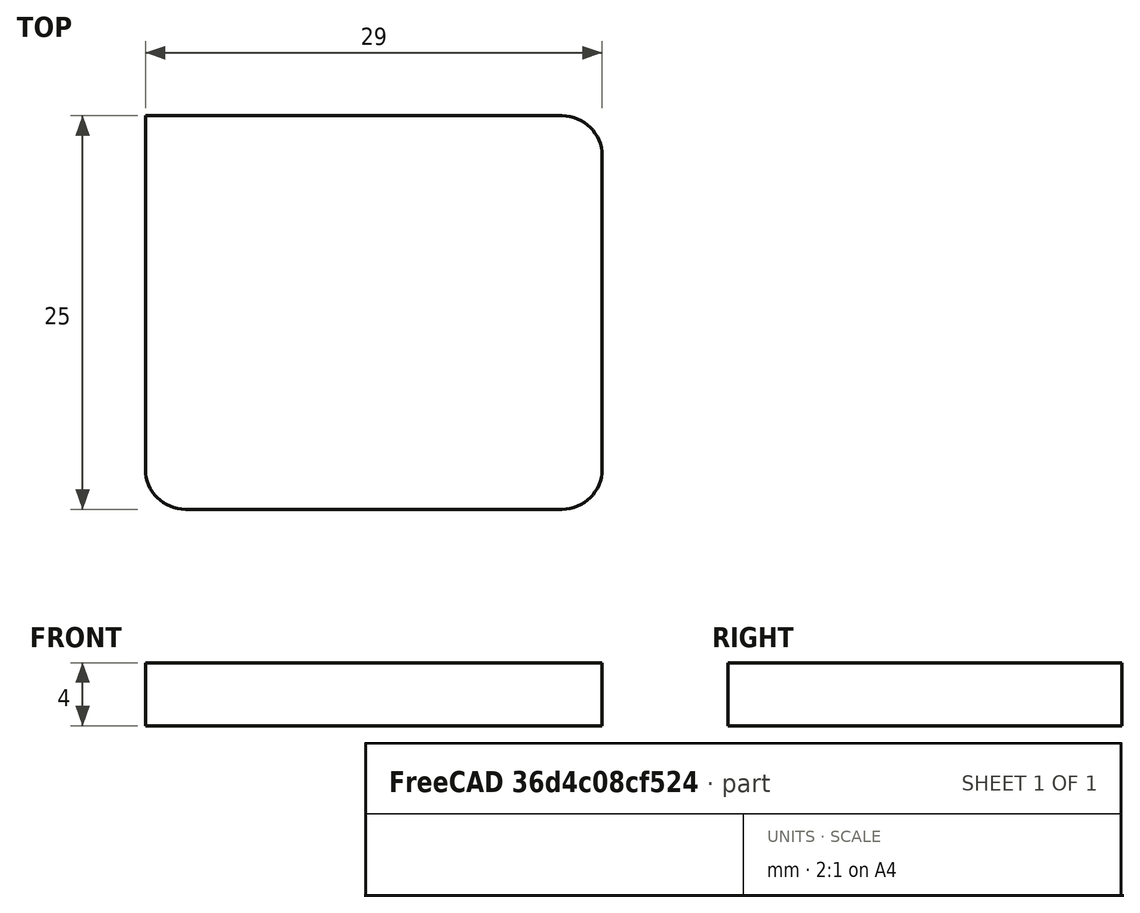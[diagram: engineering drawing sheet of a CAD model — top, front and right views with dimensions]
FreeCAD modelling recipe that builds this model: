
FCSTD DOCUMENT  (FreeCAD 1.0R39109 (Git))
Label: lora_rfm9x
License: All rights reserved
LicenseURL: http://en.wikipedia.org/wiki/All_rights_reserved
objects: Sketcher::SketchObject×1, PartDesign::Pad×1, PartDesign::Body×1
note: 6 computed .brp shape members not serialized (recipe doc carries the construction recipe); baked Part::Feature solids carry a one-line shape summary decoded from their .brp

FEATURE [Sketcher::SketchObject] Sketch
  ArcFitTolerance = 0
  AttachmentSupport = -> [XY_Plane]
  FullyConstrained = true
  MakeInternals = false
  MapMode = 5
  sketch-geometry (10):
    g0: LineSegment StartX=-14.5 StartY=12.5 StartZ=0 EndX=11.96 EndY=12.5 EndZ=0
    g1: LineSegment StartX=14.5 StartY=9.96 StartZ=0 EndX=14.5 EndY=-9.96 EndZ=0
    g2: LineSegment StartX=11.96 StartY=-12.5 StartZ=0 EndX=-11.96 EndY=-12.5 EndZ=0
    g3: LineSegment StartX=-14.5 StartY=-9.96 StartZ=0 EndX=-14.5 EndY=12.5 EndZ=0
    g4: ArcOfCircle CenterX=11.96 CenterY=-9.96 CenterZ=0 NormalX=0 NormalY=0 NormalZ=1 AngleXU=0 Radius=2.54 StartAngle=4.71239 EndAngle=6.28319
    g5: GeomPoint [constr] X=14.5 Y=-12.5 Z=0
    g6: ArcOfCircle CenterX=11.96 CenterY=9.96 CenterZ=0 NormalX=0 NormalY=0 NormalZ=1 AngleXU=0 Radius=2.54 StartAngle=0 EndAngle=1.5708
    g7: GeomPoint [constr] X=14.5 Y=12.5 Z=0
    g8: ArcOfCircle CenterX=-11.96 CenterY=-9.96 CenterZ=0 NormalX=0 NormalY=0 NormalZ=1 AngleXU=0 Radius=2.54 StartAngle=3.14159 EndAngle=4.71239
    g9: GeomPoint [constr] X=-14.5 Y=-12.5 Z=0
  constraints (23):
    c: Coincident(g3,g0)
    c: Horizontal(g0)
    c: Horizontal(g2)
    c: Vertical(g1)
    c: Vertical(g3)
    c: PointOnObject(g5,g2)
    c: PointOnObject(g5,g1)
    c: Tangent(g2,g4) = 1.5708
    c: Tangent(g1,g4) = 1.5708
    c: PointOnObject(g7,g1)
    c: PointOnObject(g7,g0)
    c: Tangent(g1,g6) = 1.5708
    c: Tangent(g0,g6) = 1.5708
    c: PointOnObject(g9,g3)
    c: PointOnObject(g9,g2)
    c: Tangent(g3,g8) = 1.5708
    c: Tangent(g2,g8) = 1.5708
    c: Symmetric(g0,g5,g-1)
    c: DistanceX(g0,g7) = 29
    c: DistanceY(g5,g7) = 25
    c: Equal(g6,g4)
    c: Equal(g6,g8)
    c: DistanceY(g2,g8) = 2.54
FEATURE [PartDesign::Pad] Pad
  Direction = (0,0,1)
  Length = 4
  Length2 = 10
  Profile = -> Sketch
  ReferenceAxis = -> Sketch [N_Axis]
  Suppressed = false
  Type = 0
FEATURE [PartDesign::Body] Body  label="Corps"
  AllowCompound = false
  Group = -> [Sketch,Pad]
  Origin = -> Origin
  Tip = -> Pad
